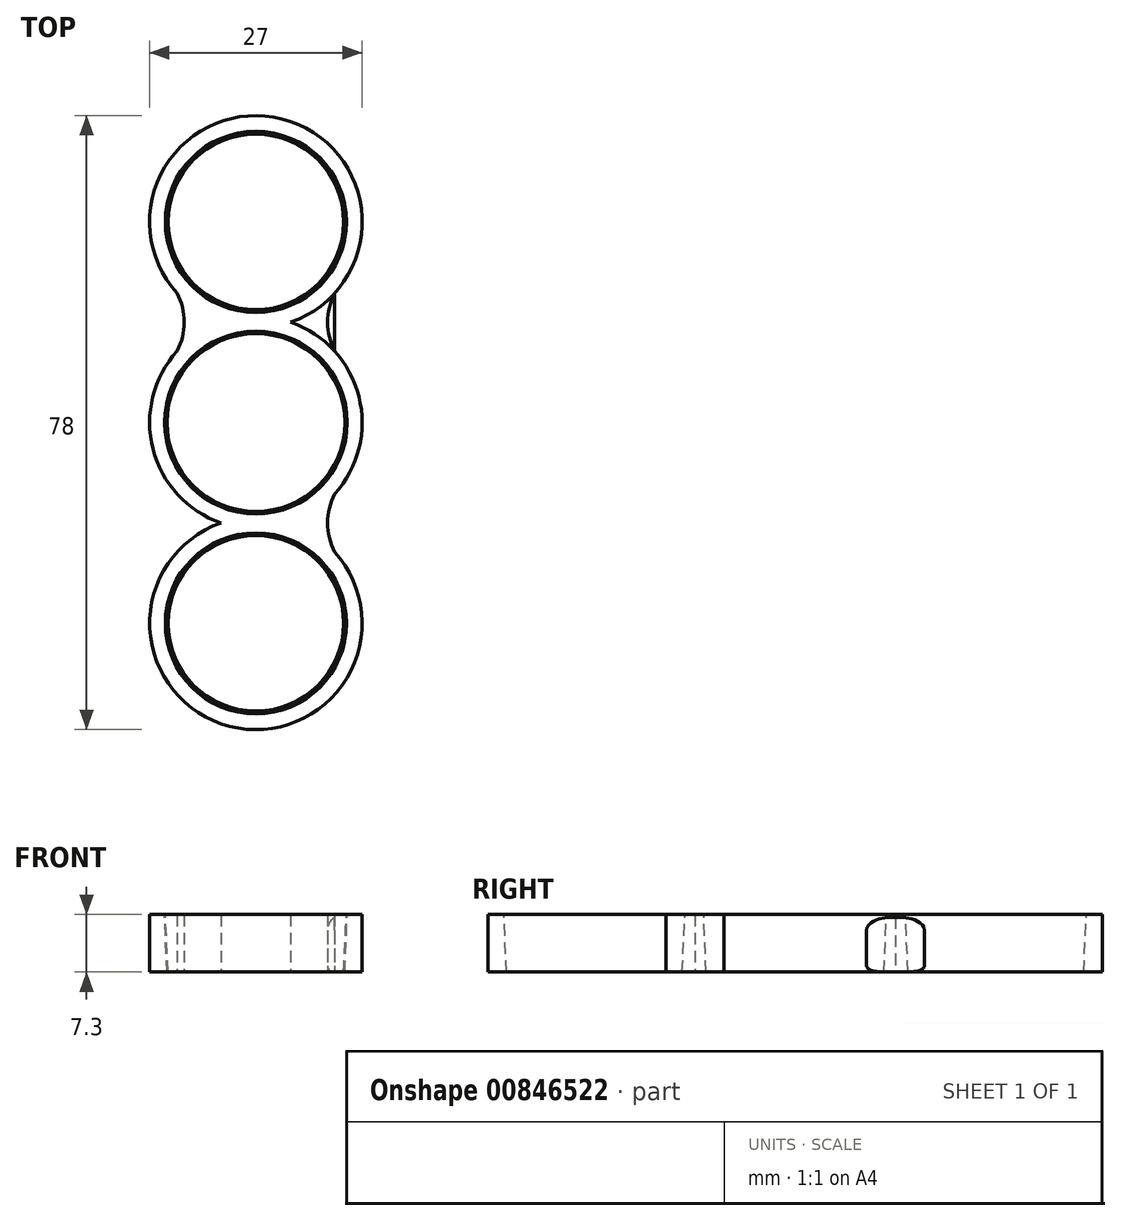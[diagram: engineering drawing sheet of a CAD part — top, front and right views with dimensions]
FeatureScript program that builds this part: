
annotation { "Feature Type Name" : "Feature", "Feature Type Description" : "" }
export const myFeature = defineFeature(function(context is Context, id is Id, definition is map)
    precondition{}
    {
        {
            var Q0;
            Q0=qCreatedBy(makeId("Top.planeOp"),FACE);
            var sketch = newSketch(context, id + "F0", { "sketchPlane" : qUnion([Q0])});
            skCircle(sketch, "E0", {"center": v(0, 0) * mm, "radius": 13.5 * mm});
            skCircle(sketch, "E1", {"center": v(0, 25.5) * mm, "radius": 13.5 * mm});
            skLineSegment(sketch, "E2", {"start": v(-10, 9.07) * mm, "end": v(-10, 16.43) * mm});
            skLineSegment(sketch, "E3", {"start": v(10, 16.43) * mm, "end": v(10, 9.07) * mm});
            skLineSegment(sketch, "E4", {"start": v(-10, 16.43) * mm, "end": v(0, 16.43) * mm});
            skLineSegment(sketch, "E5", {"start": v(0, 16.43) * mm, "end": v(10, 16.43) * mm});
            skLineSegment(sketch, "E6", {"start": v(10, 9.07) * mm, "end": v(0, 9.07) * mm});
            skLineSegment(sketch, "E7", {"start": v(0, 9.07) * mm, "end": v(-10, 9.07) * mm});
            skArc(sketch, "E8", {"start": v(-10, 9.07) * mm, "mid": v(-9.1, 12.75) * mm, "end": v(-10, 16.43) * mm});
            skArc(sketch, "E9.MirrorCS", {"start": v(10, 9.07) * mm, "mid": v(9.1, 12.75) * mm, "end": v(10, 16.43) * mm});
            skCircle(sketch, "E10.1.0", {"center": v(0, -25.5) * mm, "radius": 13.5 * mm});
            skArc(sketch, "E10.1.1", {"start": v(10, -9.07) * mm, "mid": v(9.1, -12.75) * mm, "end": v(10, -16.43) * mm});
            skArc(sketch, "E10.1.2", {"start": v(-10, -9.07) * mm, "mid": v(-9.1, -12.75) * mm, "end": v(-10, -16.43) * mm});
            skSolve(sketch);
        }
        {
            var Q0;
            {var subQ0=sQuery(id+"F0.wireOp",EDGE,"E4");Q0=makeQuery(id+"F0.imprint","IMPRINT",FACE,{"disambiguationData":[TD([[makeQuery(id+"F0.imprint","IMPRINT",EDGE,{"derivedFrom":subQ0}),1.0]])]});}
            var Q1;
            {var subQ0=sQuery(id+"F0.wireOp",EDGE,"E6");Q1=makeQuery(id+"F0.imprint","IMPRINT",FACE,{"disambiguationData":[TD([[makeQuery(id+"F0.imprint","IMPRINT",EDGE,{"derivedFrom":subQ0}),1.0]])]});}
            var Q2;
            {var subQ0=sQuery(id+"F0.wireOp",EDGE,"E10.1.2");Q2=makeQuery(id+"F0.imprint","IMPRINT",FACE,{"disambiguationData":[TD([[makeQuery(id+"F0.imprint","IMPRINT",EDGE,{"derivedFrom":subQ0}),1.0]])]});}
            var Q3;
            {var subQ0=sQuery(id+"F0.wireOp",EDGE,"E10.1.0");var subQ1=sQuery(id+"F0.wireOp",EDGE,"E0");var subQ2=makeQuery(id+"F0.imprint","INTERSECT",VERTEX,{"disambiguationData":[OD(0.0)],"derivedFrom":[subQ1,subQ0]});Q3=makeQuery(id+"F0.imprint","IMPRINT",FACE,{"disambiguationData":[TD([[makeQuery(id+"F0.imprint","IMPRINT",EDGE,{"disambiguationData":[TD([[subQ2,-1.0]])],"derivedFrom":subQ1}),1.0]])]});}
            var Q4;
            {var subQ0=sQuery(id+"F0.wireOp",EDGE,"E10.1.0");var subQ1=sQuery(id+"F0.wireOp",EDGE,"E0");var subQ2=makeQuery(id+"F0.imprint","INTERSECT",VERTEX,{"disambiguationData":[OD(0.0)],"derivedFrom":[subQ1,subQ0]});Q4=makeQuery(id+"F0.imprint","IMPRINT",FACE,{"disambiguationData":[TD([[makeQuery(id+"F0.imprint","IMPRINT",EDGE,{"disambiguationData":[TD([[subQ2,-1.0]])],"derivedFrom":subQ1}),-1.0]])]});}
            var Q5;
            {var subQ0=sQuery(id+"F0.wireOp",EDGE,"E10.1.1");Q5=makeQuery(id+"F0.imprint","IMPRINT",FACE,{"disambiguationData":[TD([[makeQuery(id+"F0.imprint","IMPRINT",EDGE,{"derivedFrom":subQ0}),-1.0]])]});}
            var Q6;
            {var subQ0=sQuery(id+"F0.wireOp",EDGE,"E4");Q6=makeQuery(id+"F0.imprint","IMPRINT",FACE,{"disambiguationData":[TD([[makeQuery(id+"F0.imprint","IMPRINT",EDGE,{"derivedFrom":subQ0}),-1.0]])]});}
            var Q7;
            {var subQ0=sQuery(id+"F0.wireOp",EDGE,"E1");var subQ1=sQuery(id+"F0.wireOp",EDGE,"E0");var subQ2=makeQuery(id+"F0.imprint","INTERSECT",VERTEX,{"disambiguationData":[OD(0.0)],"derivedFrom":[subQ1,subQ0]});Q7=makeQuery(id+"F0.imprint","IMPRINT",FACE,{"disambiguationData":[TD([[makeQuery(id+"F0.imprint","IMPRINT",EDGE,{"disambiguationData":[TD([[subQ2,-1.0]])],"derivedFrom":subQ1}),1.0]])]});}
            var Q8;
            {var subQ0=sQuery(id+"F0.wireOp",EDGE,"E6");Q8=makeQuery(id+"F0.imprint","IMPRINT",FACE,{"disambiguationData":[TD([[makeQuery(id+"F0.imprint","IMPRINT",EDGE,{"derivedFrom":subQ0}),-1.0]])]});}
            var Q9;
            {var subQ0=sQuery(id+"F0.wireOp",EDGE,"E9.MirrorCS");Q9=makeQuery(id+"F0.imprint","IMPRINT",FACE,{"disambiguationData":[TD([[makeQuery(id+"F0.imprint","IMPRINT",EDGE,{"derivedFrom":subQ0}),1.0]])]});}
            var Q10;
            {var subQ0=sQuery(id+"F0.wireOp",EDGE,"E8");Q10=makeQuery(id+"F0.imprint","IMPRINT",FACE,{"disambiguationData":[TD([[makeQuery(id+"F0.imprint","IMPRINT",EDGE,{"derivedFrom":subQ0}),-1.0]])]});}
            extrude(context, id + "F1", {"entities" : qUnion([Q0, Q1, Q2, Q3, Q4, Q5, Q6, Q7, Q8, Q9, Q10]), "depth" : 7.3 * mm, "offsetDistance" : 25 * mm});
        }
        {
            var Q0;
            Q0=makeQuery(id+"F1.opExtrude","CAP_FACE",FACE,{"disambiguationData":[OSD([sQuery(id+"F0.wireOp",EDGE,"E0"),sQuery(id+"F0.wireOp",EDGE,"E1"),sQuery(id+"F0.wireOp",EDGE,"E8"),sQuery(id+"F0.wireOp",EDGE,"E9.MirrorCS"),sQuery(id+"F0.wireOp",EDGE,"E10.1.0"),sQuery(id+"F0.wireOp",EDGE,"E10.1.1"),sQuery(id+"F0.wireOp",EDGE,"E10.1.2")])],"isStart":false});
            var sketch = newSketch(context, id + "F2", { "sketchPlane" : qUnion([Q0])});
            skCircle(sketch, "E11", {"center": v(0, 0) * mm, "radius": 11.6 * mm});
            skCircle(sketch, "E12", {"center": v(0, 25.5) * mm, "radius": 11.5 * mm});
            skCircle(sketch, "E13.1.0", {"center": v(0, -25.5) * mm, "radius": 11.5 * mm});
            skSolve(sketch);
        }
        {
            var Q0;
            Q0=makeQuery(id+"F1.opExtrude","CAP_FACE",FACE,{"disambiguationData":[OSD([sQuery(id+"F0.wireOp",EDGE,"E0"),sQuery(id+"F0.wireOp",EDGE,"E1"),sQuery(id+"F0.wireOp",EDGE,"E8"),sQuery(id+"F0.wireOp",EDGE,"E9.MirrorCS"),sQuery(id+"F0.wireOp",EDGE,"E10.1.0"),sQuery(id+"F0.wireOp",EDGE,"E10.1.1"),sQuery(id+"F0.wireOp",EDGE,"E10.1.2")])],"isStart":true});
            var sketch = newSketch(context, id + "F3", { "sketchPlane" : qUnion([Q0])});
            skCircle(sketch, "E14", {"center": v(0, 0) * mm, "radius": 11.3 * mm});
            skCircle(sketch, "E15", {"center": v(0, 25.5) * mm, "radius": 11.15 * mm});
            skCircle(sketch, "E16.1.0", {"center": v(0, -25.5) * mm, "radius": 11.15 * mm});
            skSolve(sketch);
        }
        {
            var Q1;
            Q1=makeQuery(id+"F2.imprint","IMPRINT",FACE,{"disambiguationData":[TD([[makeQuery(id+"F2.imprint","IMPRINT",EDGE,{"derivedFrom":sQuery(id+"F2.wireOp",EDGE,"E13.1.0")}),1.0]])]});
            var Q2;
            Q2=makeQuery(id+"F3.imprint","IMPRINT",FACE,{"disambiguationData":[TD([[makeQuery(id+"F3.imprint","IMPRINT",EDGE,{"derivedFrom":sQuery(id+"F3.wireOp",EDGE,"E15")}),1.0]])]});
            loft(context, id + "F4", {"operationType" : NewBodyOperationType.REMOVE, "sheetProfilesArray" : [{ "sheetProfileEntities" : qUnion([Q1]) }, { "sheetProfileEntities" : qUnion([Q2]) }]});
        }
        {
            var Q1;
            Q1=makeQuery(id+"F2.imprint","IMPRINT",FACE,{"disambiguationData":[TD([[makeQuery(id+"F2.imprint","IMPRINT",EDGE,{"derivedFrom":sQuery(id+"F2.wireOp",EDGE,"E11")}),1.0]])]});
            var Q2;
            Q2=makeQuery(id+"F3.imprint","IMPRINT",FACE,{"disambiguationData":[TD([[makeQuery(id+"F3.imprint","IMPRINT",EDGE,{"derivedFrom":sQuery(id+"F3.wireOp",EDGE,"E14")}),1.0]])]});
            loft(context, id + "F5", {"operationType" : NewBodyOperationType.REMOVE, "sheetProfilesArray" : [{ "sheetProfileEntities" : qUnion([Q1]) }, { "sheetProfileEntities" : qUnion([Q2]) }]});
        }
        {
            var Q1;
            Q1=makeQuery(id+"F2.imprint","IMPRINT",FACE,{"disambiguationData":[TD([[makeQuery(id+"F2.imprint","IMPRINT",EDGE,{"derivedFrom":sQuery(id+"F2.wireOp",EDGE,"E12")}),1.0]])]});
            var Q2;
            Q2=makeQuery(id+"F3.imprint","IMPRINT",FACE,{"disambiguationData":[TD([[makeQuery(id+"F3.imprint","IMPRINT",EDGE,{"derivedFrom":sQuery(id+"F3.wireOp",EDGE,"E16.1.0")}),1.0]])]});
            loft(context, id + "F6", {"operationType" : NewBodyOperationType.REMOVE, "sheetProfilesArray" : [{ "sheetProfileEntities" : qUnion([Q1]) }, { "sheetProfileEntities" : qUnion([Q2]) }]});
        }
        {
            var Q0;
            Q0=makeQuery(id+"F1.opExtrude","CAP_EDGE",EDGE,{"disambiguationData":[OSD([sQuery(id+"F0.wireOp",EDGE,"E1")])],"isStart":true});
            var Q1;
            Q1=makeQuery(id+"F1.opExtrude","CAP_EDGE",EDGE,{"disambiguationData":[OSD([sQuery(id+"F0.wireOp",EDGE,"E9.MirrorCS")])],"isStart":true});
            var Q2;
            {var subQ0=sQuery(id+"F0.wireOp",EDGE,"E0");Q2=makeQuery(id+"F1.opExtrude","CAP_EDGE",EDGE,{"disambiguationData":[OSD([subQ0]),TDD([makeQuery(id+"F0.imprint","IMPRINT",EDGE,{"disambiguationData":[TD([[makeQuery(id+"F0.imprint","INTERSECT",VERTEX,{"derivedFrom":[subQ0,sQuery(id+"F0.wireOp",EDGE,"E10.1.1")]}),-1.0]])],"derivedFrom":subQ0})])],"isStart":true});}
            var Q3;
            Q3=makeQuery(id+"F1.opExtrude","CAP_EDGE",EDGE,{"disambiguationData":[OSD([sQuery(id+"F0.wireOp",EDGE,"E10.1.1")])],"isStart":true});
            var Q4;
            Q4=makeQuery(id+"F1.opExtrude","CAP_EDGE",EDGE,{"disambiguationData":[OSD([sQuery(id+"F0.wireOp",EDGE,"E10.1.0")])],"isStart":true});
            var Q5;
            Q5=makeQuery(id+"F1.opExtrude","CAP_EDGE",EDGE,{"disambiguationData":[OSD([sQuery(id+"F0.wireOp",EDGE,"E10.1.2")])],"isStart":true});
            var Q6;
            {var subQ0=sQuery(id+"F0.wireOp",EDGE,"E0");Q6=makeQuery(id+"F1.opExtrude","CAP_EDGE",EDGE,{"disambiguationData":[OSD([subQ0]),TDD([makeQuery(id+"F0.imprint","IMPRINT",EDGE,{"disambiguationData":[TD([[makeQuery(id+"F0.imprint","INTERSECT",VERTEX,{"derivedFrom":[subQ0,sQuery(id+"F0.wireOp",EDGE,"E10.1.2")]}),1.0]])],"derivedFrom":subQ0})])],"isStart":true});}
            var Q7;
            Q7=makeQuery(id+"F1.opExtrude","CAP_EDGE",EDGE,{"disambiguationData":[OSD([sQuery(id+"F0.wireOp",EDGE,"E8")])],"isStart":true});
            fillet(context, id + "F7", {"entities" : qUnion([Q0, Q1, Q2, Q3, Q4, Q5, Q6, Q7]), "radius" : 0.8 * mm, "tangentPropagation" : true, "allowEdgeOverflow" : false});
        }
        {
            var Q0;
            Q0=makeQuery(id+"F1.opExtrude","CAP_EDGE",EDGE,{"disambiguationData":[OSD([sQuery(id+"F0.wireOp",EDGE,"E1")])],"isStart":false});
            var Q1;
            Q1=makeQuery(id+"F1.opExtrude","CAP_EDGE",EDGE,{"disambiguationData":[OSD([sQuery(id+"F0.wireOp",EDGE,"E8")])],"isStart":false});
            var Q2;
            {var subQ0=sQuery(id+"F0.wireOp",EDGE,"E0");Q2=makeQuery(id+"F1.opExtrude","CAP_EDGE",EDGE,{"disambiguationData":[OSD([subQ0]),TDD([makeQuery(id+"F0.imprint","IMPRINT",EDGE,{"disambiguationData":[TD([[makeQuery(id+"F0.imprint","INTERSECT",VERTEX,{"derivedFrom":[subQ0,sQuery(id+"F0.wireOp",EDGE,"E10.1.2")]}),1.0]])],"derivedFrom":subQ0})])],"isStart":false});}
            var Q3;
            Q3=makeQuery(id+"F1.opExtrude","CAP_EDGE",EDGE,{"disambiguationData":[OSD([sQuery(id+"F0.wireOp",EDGE,"E10.1.2")])],"isStart":false});
            var Q4;
            Q4=makeQuery(id+"F1.opExtrude","CAP_EDGE",EDGE,{"disambiguationData":[OSD([sQuery(id+"F0.wireOp",EDGE,"E10.1.0")])],"isStart":false});
            var Q5;
            Q5=makeQuery(id+"F1.opExtrude","CAP_EDGE",EDGE,{"disambiguationData":[OSD([sQuery(id+"F0.wireOp",EDGE,"E10.1.1")])],"isStart":false});
            var Q6;
            {var subQ0=sQuery(id+"F0.wireOp",EDGE,"E0");Q6=makeQuery(id+"F1.opExtrude","CAP_EDGE",EDGE,{"disambiguationData":[OSD([subQ0]),TDD([makeQuery(id+"F0.imprint","IMPRINT",EDGE,{"disambiguationData":[TD([[makeQuery(id+"F0.imprint","INTERSECT",VERTEX,{"derivedFrom":[subQ0,sQuery(id+"F0.wireOp",EDGE,"E10.1.1")]}),-1.0]])],"derivedFrom":subQ0})])],"isStart":false});}
            var Q7;
            Q7=makeQuery(id+"F1.opExtrude","CAP_EDGE",EDGE,{"disambiguationData":[OSD([sQuery(id+"F0.wireOp",EDGE,"E9.MirrorCS")])],"isStart":false});
            fillet(context, id + "F8", {"entities" : qUnion([Q0, Q1, Q2, Q3, Q4, Q5, Q6, Q7]), "radius" : 2 * mm, "tangentPropagation" : true, "allowEdgeOverflow" : false});
        }
    });
